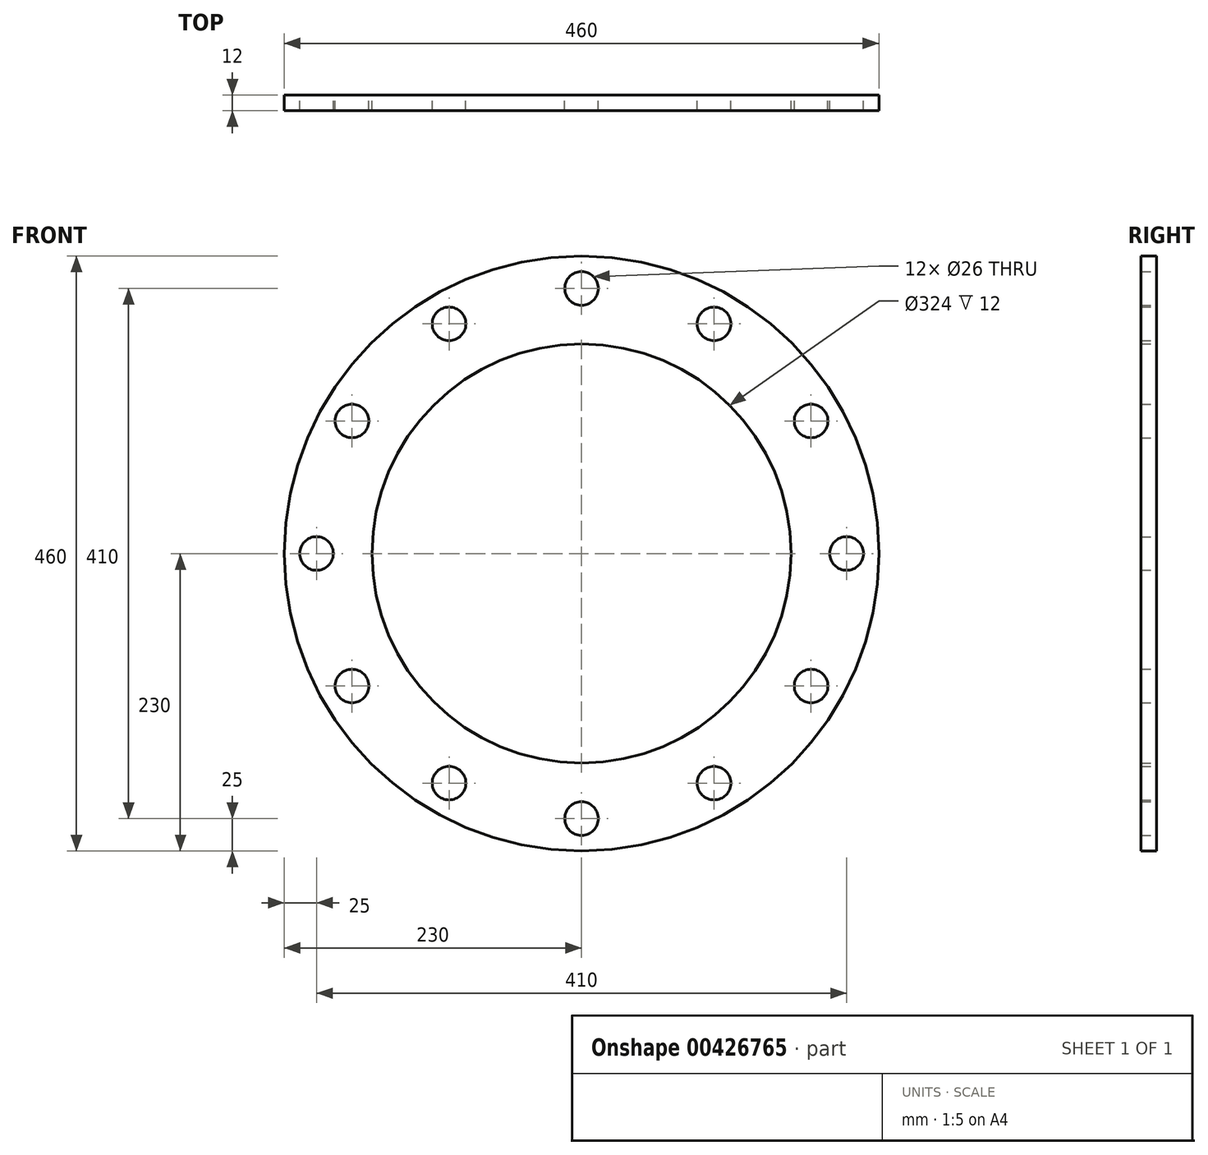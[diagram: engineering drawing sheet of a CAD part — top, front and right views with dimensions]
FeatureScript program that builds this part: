
annotation { "Feature Type Name" : "Feature", "Feature Type Description" : "" }
export const myFeature = defineFeature(function(context is Context, id is Id, definition is map)
    precondition{}
    {
        {
            var Q0;
            Q0=qCreatedBy(makeId("Front.planeOp"),FACE);
            var sketch = newSketch(context, id + "F0", { "sketchPlane" : qUnion([Q0])});
            skCircle(sketch, "E0", {"center": v(0, 0) * mm, "radius": 230 * mm});
            skCircle(sketch, "E1", {"center": v(0, 0) * mm, "radius": 205 * mm, "construction": true});
            skCircle(sketch, "E2", {"center": v(0, 205) * mm, "radius": 13 * mm});
            skCircle(sketch, "E3.1.0", {"center": v(-102.5, 177.54) * mm, "radius": 13 * mm});
            skCircle(sketch, "E3.2.0", {"center": v(-177.54, 102.5) * mm, "radius": 13 * mm});
            skCircle(sketch, "E4.1.3.0", {"center": v(-205, 0) * mm, "radius": 13 * mm});
            skCircle(sketch, "E4.1.4.0", {"center": v(-177.54, -102.5) * mm, "radius": 13 * mm});
            skCircle(sketch, "E4.1.5.0", {"center": v(-102.5, -177.54) * mm, "radius": 13 * mm});
            skCircle(sketch, "E4.1.6.0", {"center": v(0, -205) * mm, "radius": 13 * mm});
            skCircle(sketch, "E4.1.7.0", {"center": v(102.5, -177.54) * mm, "radius": 13 * mm});
            skCircle(sketch, "E4.1.8.0", {"center": v(177.54, -102.5) * mm, "radius": 13 * mm});
            skCircle(sketch, "E4.1.9.0", {"center": v(205, 0) * mm, "radius": 13 * mm});
            skCircle(sketch, "E4.1.10.0", {"center": v(177.54, 102.5) * mm, "radius": 13 * mm});
            skCircle(sketch, "E4.1.11.0", {"center": v(102.5, 177.54) * mm, "radius": 13 * mm});
            skCircle(sketch, "E5", {"center": v(0, 0) * mm, "radius": 162 * mm});
            skSolve(sketch);
        }
        {
            var Q0;
            Q0=makeQuery(id+"F0.imprint","IMPRINT",FACE,{"disambiguationData":[TD([[makeQuery(id+"F0.imprint","IMPRINT",EDGE,{"derivedFrom":sQuery(id+"F0.wireOp",EDGE,"E0")}),1.0]])]});
            extrude(context, id + "F1", {"entities" : qUnion([Q0]), "depth" : 12 * mm});
        }
    });
